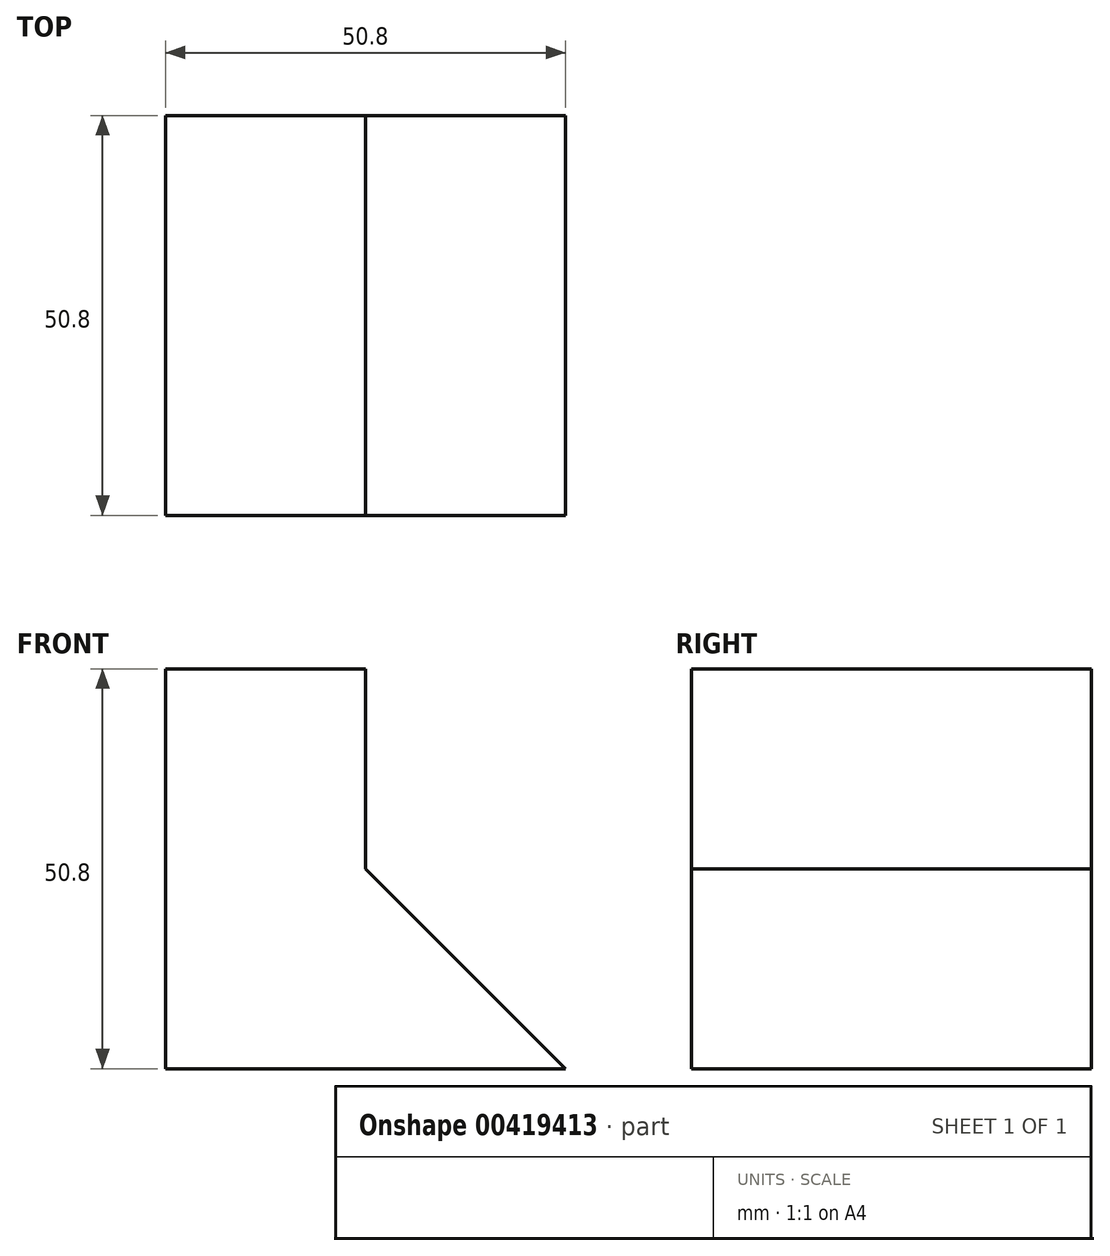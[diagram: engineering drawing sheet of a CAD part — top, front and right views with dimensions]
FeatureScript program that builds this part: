
annotation { "Feature Type Name" : "Feature", "Feature Type Description" : "" }
export const myFeature = defineFeature(function(context is Context, id is Id, definition is map)
    precondition{}
    {
        {
            var Q0;
            Q0=qCreatedBy(makeId("Front.planeOp"),FACE);
            var sketch = newSketch(context, id + "F0", { "sketchPlane" : qUnion([Q0])});
            skLineSegment(sketch, "E0", {"start": v(-65.97, 58.44) * mm, "end": v(-65.97, 7.64) * mm});
            skLineSegment(sketch, "E1", {"start": v(-65.97, 7.64) * mm, "end": v(-15.17, 7.64) * mm});
            skLineSegment(sketch, "E2", {"start": v(-65.97, 58.44) * mm, "end": v(-40.57, 58.44) * mm});
            skLineSegment(sketch, "E3", {"start": v(-40.57, 58.44) * mm, "end": v(-40.57, 33.04) * mm});
            skLineSegment(sketch, "E4", {"start": v(-40.57, 33.04) * mm, "end": v(-15.17, 7.64) * mm});
            skSolve(sketch);
        }
        {
            var Q0;
            Q0 = qSketchRegion(id + "F0", true);
            extrude(context, id + "F1", {"entities" : qUnion([Q0]), "depth" : 50.8 * mm});
        }
    });
